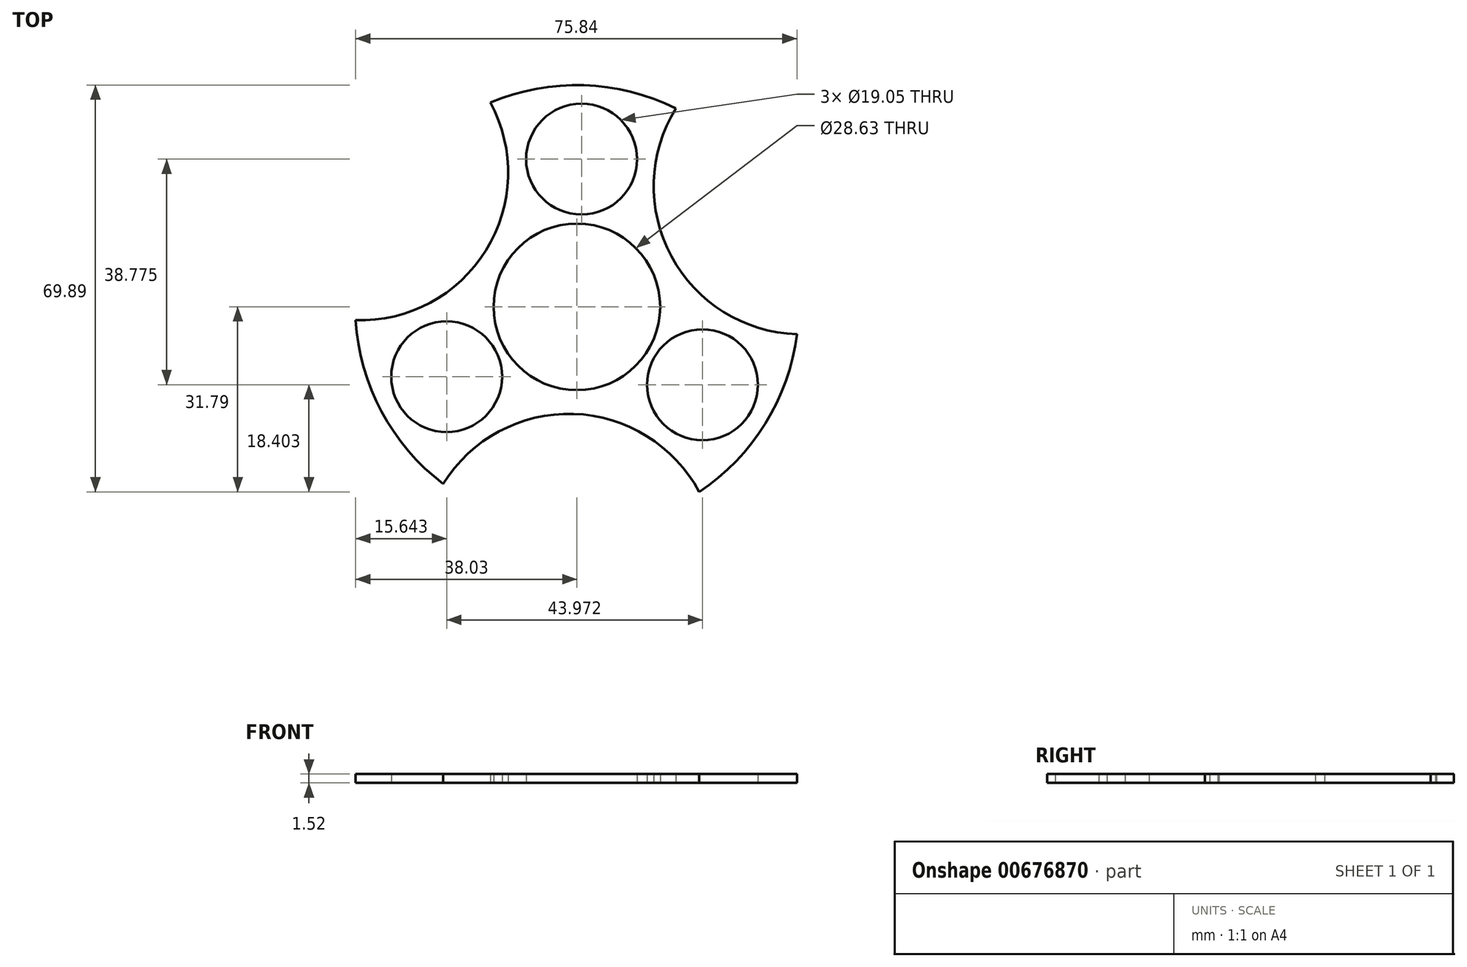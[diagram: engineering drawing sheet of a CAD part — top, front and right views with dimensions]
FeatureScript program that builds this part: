
annotation { "Feature Type Name" : "Feature", "Feature Type Description" : "" }
export const myFeature = defineFeature(function(context is Context, id is Id, definition is map)
    precondition{}
    {
        {
            var Q0;
            Q0=qCreatedBy(makeId("Top.planeOp"),FACE);
            var sketch = newSketch(context, id + "F0", { "sketchPlane" : qUnion([Q0])});
            skCircle(sketch, "E0.cCircle", {"center": v(0, 0) * mm, "radius": 38.1 * mm});
            skPoint(sketch, "E0.0.midPoint", {"position": v(-32.38, 20.08) * mm});
            skLineSegment(sketch, "E1", {"start": v(-43.97, 1.39) * mm, "end": v(23.19, 37.39) * mm, "construction": true});
            skLineSegment(sketch, "E2", {"start": v(20.78, -38.77) * mm, "end": v(23.19, 37.39) * mm, "construction": true});
            skLineSegment(sketch, "E3", {"start": v(20.78, -38.77) * mm, "end": v(-43.97, 1.39) * mm, "construction": true});
            skLineSegment(sketch, "E4", {"start": v(-20.78, 38.77) * mm, "end": v(-23.19, -37.39) * mm, "construction": true});
            skLineSegment(sketch, "E5", {"start": v(43.97, -1.39) * mm, "end": v(-23.19, -37.39) * mm, "construction": true});
            skLineSegment(sketch, "E6", {"start": v(-20.78, 38.77) * mm, "end": v(43.97, -1.39) * mm, "construction": true});
            skCircle(sketch, "E7", {"center": v(0.8, 25.39) * mm, "radius": 9.53 * mm});
            skCircle(sketch, "E8", {"center": v(21.59, -13.39) * mm, "radius": 9.53 * mm});
            skCircle(sketch, "E9", {"center": v(-22.39, -12) * mm, "radius": 9.53 * mm});
            skCircle(sketch, "E10", {"center": v(0, 0) * mm, "radius": 14.31 * mm});
            skArc(sketch, "E11", {"start": v(-38.03, -2.3) * mm, "mid": v(-15.64, 9.7) * mm, "end": v(-14.84, 35.09) * mm});
            skArc(sketch, "E12", {"start": v(17.03, 34.08) * mm, "mid": v(16.22, 8.7) * mm, "end": v(37.81, -4.7) * mm});
            skArc(sketch, "E13", {"start": v(21, -31.79) * mm, "mid": v(-0.58, -18.4) * mm, "end": v(-22.97, -30.4) * mm});
            skSolve(sketch);
        }
        {
            var Q0;
            Q0=makeQuery(id+"F0.imprint","IMPRINT",FACE,{"disambiguationData":[TD([[makeQuery(id+"F0.imprint","IMPRINT",EDGE,{"derivedFrom":sQuery(id+"F0.wireOp",EDGE,"E7")}),-1.0]])]});
            extrude(context, id + "F1", {"entities" : qUnion([Q0]), "depth" : 1.52 * mm, "offsetDistance" : 25.4 * mm});
        }
    });
